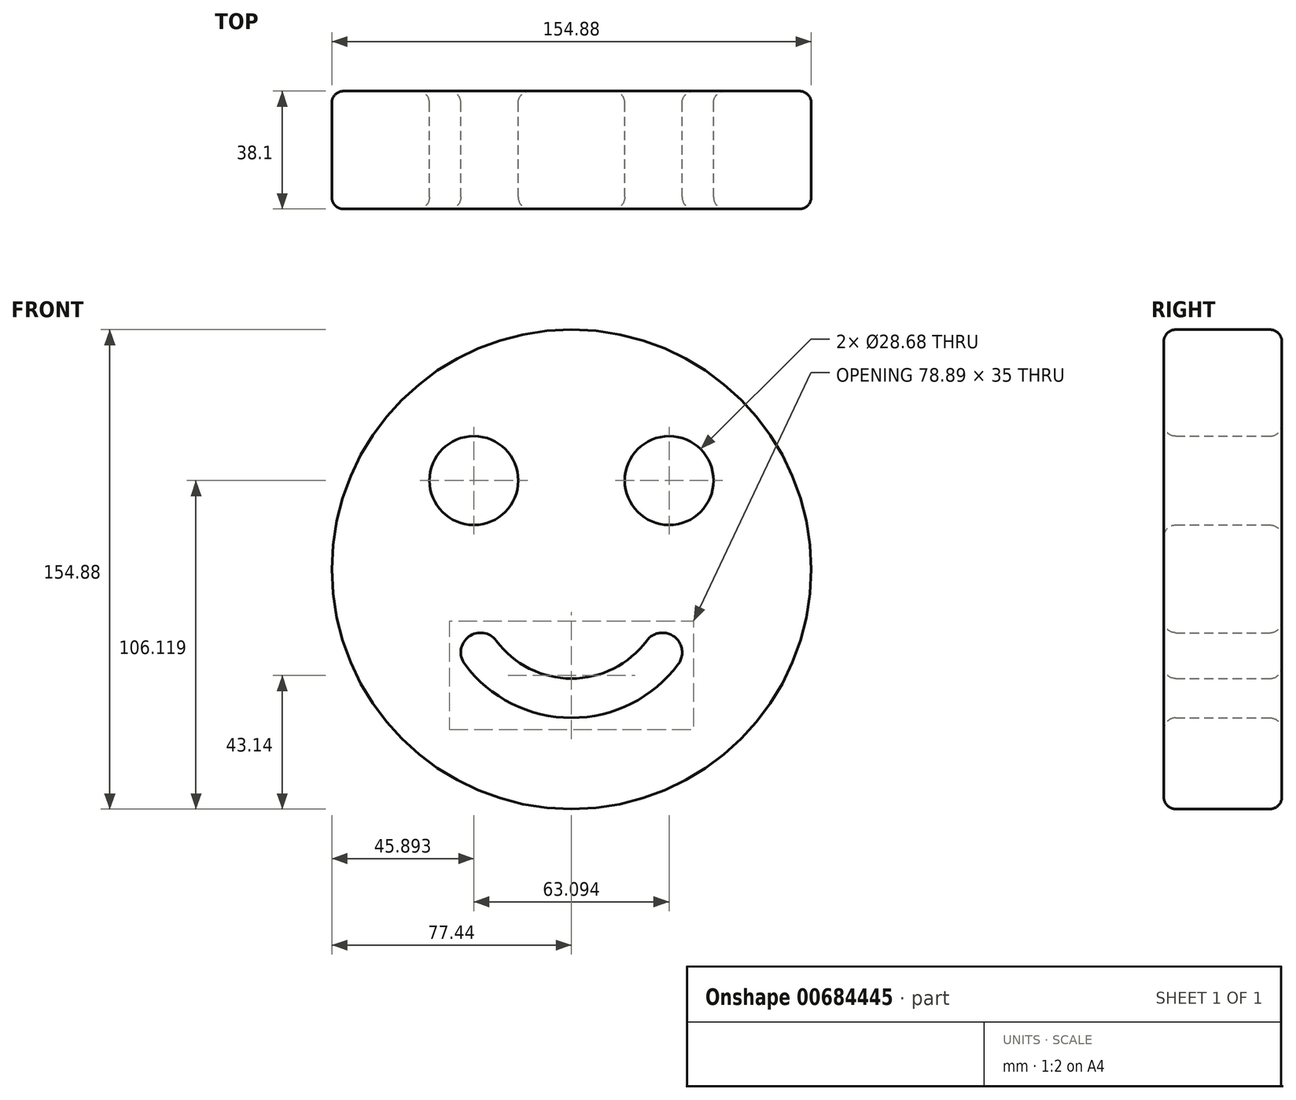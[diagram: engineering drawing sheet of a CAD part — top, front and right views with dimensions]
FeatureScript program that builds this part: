
annotation { "Feature Type Name" : "Feature", "Feature Type Description" : "" }
export const myFeature = defineFeature(function(context is Context, id is Id, definition is map)
    precondition{}
    {
        {
            var Q0;
            Q0=qCreatedBy(makeId("Front.planeOp"),FACE);
            var sketch = newSketch(context, id + "F0", { "sketchPlane" : qUnion([Q0])});
            skCircle(sketch, "E0", {"center": v(0, 0) * mm, "radius": 77.44 * mm});
            skCircle(sketch, "E1", {"center": v(-31.55, 28.68) * mm, "radius": 14.34 * mm});
            skCircle(sketch, "E2", {"center": v(31.55, 28.68) * mm, "radius": 14.34 * mm});
            skArc(sketch, "E3", {"start": v(-34.5, -30.63) * mm, "mid": v(0, -48) * mm, "end": v(34.5, -30.63) * mm});
            skArc(sketch, "E4.0", {"start": v(-24.3, -23.06) * mm, "mid": v(0, -35.3) * mm, "end": v(24.3, -23.06) * mm});
            skArc(sketch, "E5", {"start": v(-34.5, -30.63) * mm, "mid": v(-33.18, -21.75) * mm, "end": v(-24.3, -23.06) * mm});
            skArc(sketch, "E6", {"start": v(24.3, -23.06) * mm, "mid": v(33.18, -21.75) * mm, "end": v(34.5, -30.63) * mm});
            skSolve(sketch);
        }
        {
            var Q0;
            Q0=makeQuery(id+"F0.imprint","IMPRINT",FACE,{"disambiguationData":[TD([[makeQuery(id+"F0.imprint","IMPRINT",EDGE,{"derivedFrom":sQuery(id+"F0.wireOp",EDGE,"E0")}),1.0]])]});
            extrude(context, id + "F1", {"entities" : qUnion([Q0]), "depth" : 38.1 * mm, "offsetDistance" : 25.4 * mm});
        }
        {
            var Q0;
            Q0=makeQuery(id+"F1.opExtrude","CAP_EDGE",EDGE,{"disambiguationData":[OSD([sQuery(id+"F0.wireOp",EDGE,"E4.0")])],"isStart":false});
            var Q1;
            Q1=makeQuery(id+"F1.opExtrude","CAP_EDGE",EDGE,{"disambiguationData":[OSD([sQuery(id+"F0.wireOp",EDGE,"E5")])],"isStart":false});
            fillet(context, id + "F2", {"entities" : qUnion([Q0, Q1]), "radius" : 3.8 * mm, "tangentPropagation" : true, "allowEdgeOverflow" : false});
        }
        {
            var Q0;
            Q0=makeQuery(id+"F1.opExtrude","CAP_EDGE",EDGE,{"disambiguationData":[OSD([sQuery(id+"F0.wireOp",EDGE,"E1")])],"isStart":false});
            var Q1;
            Q1=makeQuery(id+"F1.opExtrude","CAP_EDGE",EDGE,{"disambiguationData":[OSD([sQuery(id+"F0.wireOp",EDGE,"E2")])],"isStart":false});
            var Q2;
            Q2=makeQuery(id+"F1.opExtrude","CAP_EDGE",EDGE,{"disambiguationData":[OSD([sQuery(id+"F0.wireOp",EDGE,"E0")])],"isStart":false});
            var Q3;
            Q3=makeQuery(id+"F1.opExtrude","CAP_EDGE",EDGE,{"disambiguationData":[OSD([sQuery(id+"F0.wireOp",EDGE,"E0")])],"isStart":true});
            var Q4;
            Q4=makeQuery(id+"F1.opExtrude","CAP_EDGE",EDGE,{"disambiguationData":[OSD([sQuery(id+"F0.wireOp",EDGE,"E4.0")])],"isStart":true});
            var Q5;
            Q5=makeQuery(id+"F1.opExtrude","CAP_EDGE",EDGE,{"disambiguationData":[OSD([sQuery(id+"F0.wireOp",EDGE,"E2")])],"isStart":true});
            var Q6;
            Q6=makeQuery(id+"F1.opExtrude","CAP_EDGE",EDGE,{"disambiguationData":[OSD([sQuery(id+"F0.wireOp",EDGE,"E1")])],"isStart":true});
            fillet(context, id + "F3", {"entities" : qUnion([Q0, Q1, Q2, Q3, Q4, Q5, Q6]), "radius" : 3.8 * mm, "tangentPropagation" : true, "allowEdgeOverflow" : false});
        }
    });
